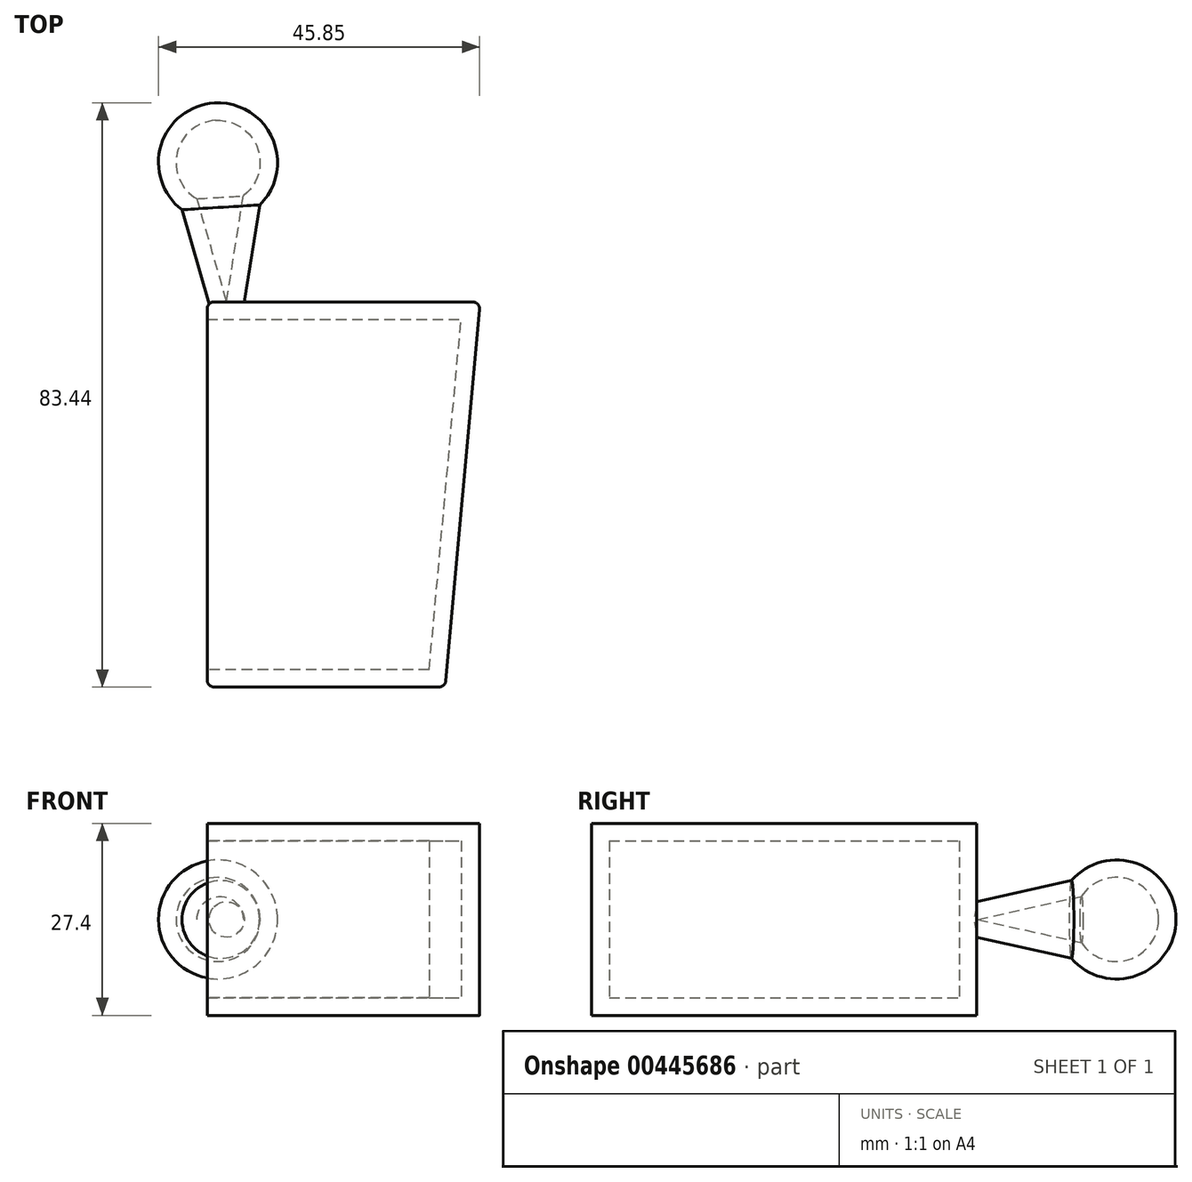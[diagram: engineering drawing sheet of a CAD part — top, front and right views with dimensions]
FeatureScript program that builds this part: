
annotation { "Feature Type Name" : "Feature", "Feature Type Description" : "" }
export const myFeature = defineFeature(function(context is Context, id is Id, definition is map)
    precondition{}
    {
        {
            var Q0;
            Q0=qCreatedBy(makeId("Top.planeOp"),FACE);
            var sketch = newSketch(context, id + "F0", { "sketchPlane" : qUnion([Q0])});
            skLineSegment(sketch, "E0", {"start": v(12.97, -52.58) * mm, "end": v(-19.12, -52.58) * mm});
            skLineSegment(sketch, "E1", {"start": v(-19.12, 2.42) * mm, "end": v(17.79, 2.42) * mm});
            skLineSegment(sketch, "E2", {"start": v(13.96, -51.67) * mm, "end": v(18.78, 1.33) * mm});
            skLineSegment(sketch, "E3", {"start": v(-20.12, -51.58) * mm, "end": v(-20.12, 1.42) * mm});
            skPoint(sketch, "E4.visualSharp", {"position": v(13.88, -52.58) * mm});
            skArc(sketch, "E4.filletArc", {"start": v(12.97, -52.58) * mm, "mid": v(13.64, -52.31) * mm, "end": v(13.96, -51.67) * mm});
            skPoint(sketch, "E5.visualSharp", {"position": v(-20.12, -52.58) * mm});
            skArc(sketch, "E5.filletArc", {"start": v(-20.12, -51.58) * mm, "mid": v(-19.82, -52.28) * mm, "end": v(-19.12, -52.58) * mm});
            skPoint(sketch, "E6.visualSharp", {"position": v(18.88, 2.42) * mm});
            skArc(sketch, "E6.filletArc", {"start": v(18.78, 1.33) * mm, "mid": v(18.53, 2.1) * mm, "end": v(17.79, 2.42) * mm});
            skPoint(sketch, "E7.visualSharp", {"position": v(-20.12, 2.42) * mm});
            skArc(sketch, "E7.filletArc", {"start": v(-19.12, 2.42) * mm, "mid": v(-19.82, 2.13) * mm, "end": v(-20.12, 1.42) * mm});
            skPoint(sketch, "E8.center.orphan", {"position": v(-16, 62.07) * mm});
            skPoint(sketch, "E9.orphan", {"position": v(-16, 71.07) * mm});
            skSolve(sketch);
        }
        {
            var Q0;
            Q0=makeQuery(id+"F0.imprint","IMPRINT",FACE,{"disambiguationData":[TD([[makeQuery(id+"F0.imprint","IMPRINT",EDGE,{"derivedFrom":sQuery(id+"F0.wireOp",EDGE,"E0")}),-1.0]])]});
            extrude(context, id + "F1", {"entities" : qUnion([Q0]), "endBound" : BoundingType.SYMMETRIC, "depth" : 27.4 * mm, "offsetDistance" : 25 * mm});
        }
        {
            var Q0;
            Q0=makeQuery(id+"F1.opExtrude","SWEPT_FACE",FACE,{"disambiguationData":[OSD([sQuery(id+"F0.wireOp",EDGE,"E1")])]});
            var sketch = newSketch(context, id + "F2", { "sketchPlane" : qUnion([Q0])});
            skCircle(sketch, "E10", {"center": v(19.12, 0) * mm, "radius": 5 * mm});
            skPoint(sketch, "E11", {"position": v(-17.79, 0) * mm});
            skSolve(sketch);
        }
        {
            var Q0;
            Q0=qCreatedBy(makeId("Top.planeOp"),FACE);
            var sketch = newSketch(context, id + "F3", { "sketchPlane" : qUnion([Q0])});
            skArc(sketch, "E12", {"start": v(-12.63, 16.28) * mm, "mid": v(-10.8, 25.8) * mm, "end": v(-19.09, 30.85) * mm});
            skLineSegment(sketch, "E13", {"start": v(-12.63, 16.28) * mm, "end": v(-14.83, 2.42) * mm});
            skLineSegment(sketch, "E14", {"start": v(-17.34, 2.42) * mm, "end": v(-19.09, 30.85) * mm});
            skLineSegment(sketch, "E15", {"start": v(-14.83, 2.42) * mm, "end": v(-17.34, 2.42) * mm});
            skSolve(sketch);
        }
        {
            var Q0;
            Q0=makeQuery(id+"F3.imprint","IMPRINT",FACE,{"disambiguationData":[TD([[makeQuery(id+"F3.imprint","IMPRINT",EDGE,{"derivedFrom":sQuery(id+"F3.wireOp",EDGE,"E12")}),1.0]])]});
            var Q1;
            Q1=sQuery(id+"F3.wireOp",EDGE,"E12");
            var Q2;
            Q2=sQuery(id+"F3.wireOp",EDGE,"E13");
            var Q3;
            Q3=sQuery(id+"F3.wireOp",EDGE,"E14");
            revolve(context, id + "F4", {"operationType" : NewBodyOperationType.ADD, "surfaceOperationType" : NewSurfaceOperationType.ADD, "entities" : qUnion([Q0]), "surfaceEntities" : qUnion([Q1, Q2]), "axis" : qUnion([Q3]), "revolveType" : RevolveType.FULL});
        }
        {
            var Q0;
            Q0=makeQuery(id+"F1.opExtrude","SWEPT_FACE",FACE,{"disambiguationData":[OSD([sQuery(id+"F0.wireOp",EDGE,"E3")])]});
            shell(context, id + "F5", {"entities" : qUnion([Q0]), "thickness" : 2.5 * mm});
        }
    });
